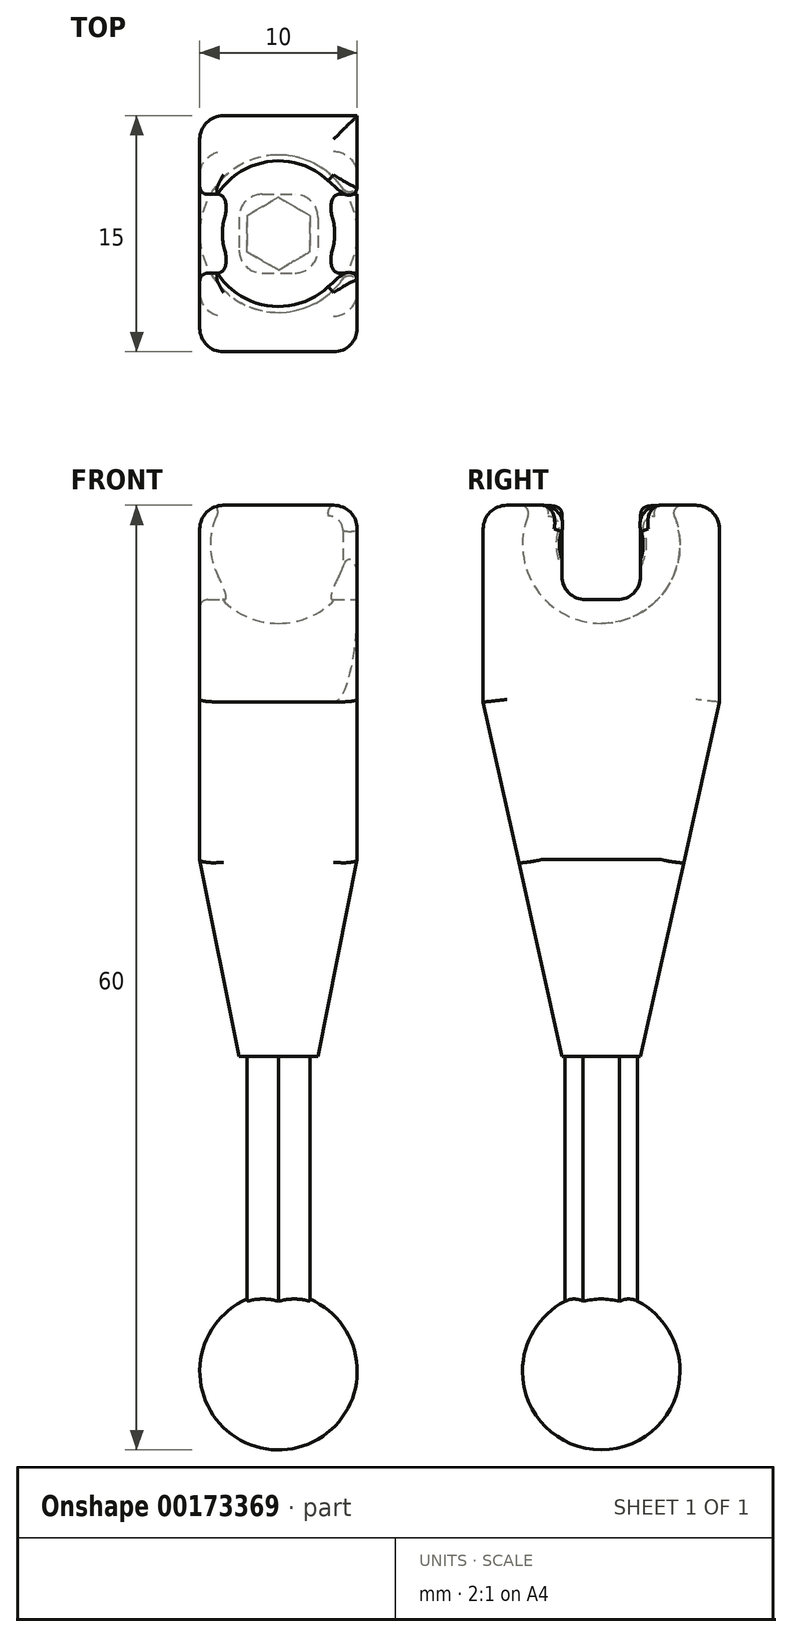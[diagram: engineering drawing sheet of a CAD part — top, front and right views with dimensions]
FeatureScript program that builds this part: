
annotation { "Feature Type Name" : "Feature", "Feature Type Description" : "" }
export const myFeature = defineFeature(function(context is Context, id is Id, definition is map)
    precondition{}
    {
        {
            var Q0;
            Q0=qCreatedBy(makeId("Right.planeOp"),FACE);
            var sketch = newSketch(context, id + "F0", { "sketchPlane" : qUnion([Q0])});
            skLineSegment(sketch, "E0.bottom", {"start": v(-7.5, 50.25) * mm, "end": v(7.5, 50.25) * mm});
            skLineSegment(sketch, "E0.top", {"start": v(-7.5, 15.25) * mm, "end": v(7.5, 15.25) * mm});
            skLineSegment(sketch, "E0.left", {"start": v(-7.5, 50.25) * mm, "end": v(-7.5, 15.25) * mm});
            skLineSegment(sketch, "E0.right", {"start": v(7.5, 50.25) * mm, "end": v(7.5, 15.25) * mm});
            skSolve(sketch);
        }
        {
            var Q0;
            Q0 = qSketchRegion(id + "F0", true);
            extrude(context, id + "F1", {"entities" : qUnion([Q0]), "endBound" : BoundingType.SYMMETRIC, "depth" : 10 * mm});
        }
        {
            var Q0;
            Q0=makeQuery(id+"F1.opExtrude","CAP_FACE",FACE,{"disambiguationData":[OSD([sQuery(id+"F0.wireOp",EDGE,"E0.bottom"),sQuery(id+"F0.wireOp",EDGE,"E0.top"),sQuery(id+"F0.wireOp",EDGE,"E0.left"),sQuery(id+"F0.wireOp",EDGE,"E0.right")])],"isStart":false});
            var sketch = newSketch(context, id + "F2", { "sketchPlane" : qUnion([Q0])});
            skLineSegment(sketch, "E1", {"start": v(-7.5, 15.25) * mm, "end": v(-7.5, 37.75) * mm});
            skLineSegment(sketch, "E2", {"start": v(-7.5, 37.75) * mm, "end": v(-2.5, 15.25) * mm});
            skLineSegment(sketch, "E3", {"start": v(-2.5, 15.25) * mm, "end": v(-7.5, 15.25) * mm});
            skLineSegment(sketch, "E4", {"start": v(0, 50.25) * mm, "end": v(0, 15.25) * mm, "construction": true});
            skLineSegment(sketch, "E5.MirrorCS", {"start": v(7.5, 15.25) * mm, "end": v(7.5, 37.75) * mm});
            skLineSegment(sketch, "E6.MirrorCS", {"start": v(7.5, 37.75) * mm, "end": v(2.5, 15.25) * mm});
            skLineSegment(sketch, "E7.MirrorCS", {"start": v(2.5, 15.25) * mm, "end": v(7.5, 15.25) * mm});
            skSolve(sketch);
        }
        {
            var Q0;
            Q0 = qSketchRegion(id + "F2", true);
            extrude(context, id + "F3", {"entities" : qUnion([Q0]), "operationType" : NewBodyOperationType.REMOVE, "endBound" : BoundingType.SYMMETRIC, "oppositeDirection" : true, "depth" : 25 * mm});
        }
        {
            var Q0;
            Q0=qCreatedBy(makeId("Front.planeOp"),FACE);
            var sketch = newSketch(context, id + "F4", { "sketchPlane" : qUnion([Q0])});
            skLineSegment(sketch, "E8", {"start": v(5, 27.75) * mm, "end": v(5, 15.25) * mm});
            skLineSegment(sketch, "E9", {"start": v(5, 15.25) * mm, "end": v(2.5, 15.25) * mm});
            skLineSegment(sketch, "E10", {"start": v(2.5, 15.25) * mm, "end": v(5, 27.75) * mm});
            skLineSegment(sketch, "E11", {"start": v(0, 10.16) * mm, "end": v(0, 28) * mm, "construction": true});
            skLineSegment(sketch, "E12.MirrorCS", {"start": v(-5, 27.75) * mm, "end": v(-5, 15.25) * mm});
            skLineSegment(sketch, "E13.MirrorCS", {"start": v(-5, 15.25) * mm, "end": v(-2.5, 15.25) * mm});
            skLineSegment(sketch, "E14.MirrorCS", {"start": v(-2.5, 15.25) * mm, "end": v(-5, 27.75) * mm});
            skSolve(sketch);
        }
        {
            var Q0;
            Q0 = qSketchRegion(id + "F4", true);
            extrude(context, id + "F5", {"entities" : qUnion([Q0]), "operationType" : NewBodyOperationType.REMOVE, "endBound" : BoundingType.SYMMETRIC, "oppositeDirection" : true, "depth" : 50 * mm});
        }
        {
            var Q0;
            Q0=makeQuery(id+"F3.boolean.opBoolean","INTERSECT",EDGE,{"derivedFrom":[makeQuery(id+"F1.opExtrude","CAP_FACE",FACE,{"disambiguationData":[OSD([sQuery(id+"F0.wireOp",EDGE,"E0.bottom"),sQuery(id+"F0.wireOp",EDGE,"E0.top"),sQuery(id+"F0.wireOp",EDGE,"E0.left"),sQuery(id+"F0.wireOp",EDGE,"E0.right")])],"isStart":true}),makeQuery(id+"F3.opExtrude","SWEPT_FACE",FACE,{"disambiguationData":[OSD([sQuery(id+"F2.wireOp",EDGE,"E2")])]})]});
            var Q1;
            Q1=makeQuery(id+"F5.boolean.opBoolean","INTERSECT",EDGE,{"derivedFrom":[makeQuery(id+"F3.boolean.opBoolean","COPY",FACE,{"derivedFrom":makeQuery(id+"F3.opExtrude","SWEPT_FACE",FACE,{"disambiguationData":[OSD([sQuery(id+"F2.wireOp",EDGE,"E2")])]})}),makeQuery(id+"F5.opExtrude","SWEPT_FACE",FACE,{"disambiguationData":[OSD([sQuery(id+"F4.wireOp",EDGE,"E14.MirrorCS")])]})]});
            var Q2;
            Q2=makeQuery(id+"F5.boolean.opBoolean","INTERSECT",EDGE,{"derivedFrom":[makeQuery(id+"F3.boolean.opBoolean","COPY",FACE,{"derivedFrom":makeQuery(id+"F3.opExtrude","SWEPT_FACE",FACE,{"disambiguationData":[OSD([sQuery(id+"F2.wireOp",EDGE,"E2")])]})}),makeQuery(id+"F5.opExtrude","SWEPT_FACE",FACE,{"disambiguationData":[OSD([sQuery(id+"F4.wireOp",EDGE,"E10")])]})]});
            var Q3;
            Q3=makeQuery(id+"F3.boolean.opBoolean","INTERSECT",EDGE,{"derivedFrom":[makeQuery(id+"F1.opExtrude","CAP_FACE",FACE,{"disambiguationData":[OSD([sQuery(id+"F0.wireOp",EDGE,"E0.bottom"),sQuery(id+"F0.wireOp",EDGE,"E0.top"),sQuery(id+"F0.wireOp",EDGE,"E0.left"),sQuery(id+"F0.wireOp",EDGE,"E0.right")])],"isStart":false}),makeQuery(id+"F3.opExtrude","SWEPT_FACE",FACE,{"disambiguationData":[OSD([sQuery(id+"F2.wireOp",EDGE,"E2")])]})]});
            var Q4;
            Q4=makeQuery(id+"F1.opExtrude","CAP_EDGE",EDGE,{"disambiguationData":[OSD([sQuery(id+"F0.wireOp",EDGE,"E0.left")])],"isStart":false});
            var Q5;
            Q5=makeQuery(id+"F1.opExtrude","CAP_EDGE",EDGE,{"disambiguationData":[OSD([sQuery(id+"F0.wireOp",EDGE,"E0.left")])],"isStart":true});
            var Q6;
            Q6=makeQuery(id+"F1.opExtrude","CAP_EDGE",EDGE,{"disambiguationData":[OSD([sQuery(id+"F0.wireOp",EDGE,"E0.right")])],"isStart":true});
            var Q7;
            Q7=makeQuery(id+"F3.boolean.opBoolean","INTERSECT",EDGE,{"derivedFrom":[makeQuery(id+"F1.opExtrude","CAP_FACE",FACE,{"disambiguationData":[OSD([sQuery(id+"F0.wireOp",EDGE,"E0.bottom"),sQuery(id+"F0.wireOp",EDGE,"E0.top"),sQuery(id+"F0.wireOp",EDGE,"E0.left"),sQuery(id+"F0.wireOp",EDGE,"E0.right")])],"isStart":true}),makeQuery(id+"F3.opExtrude","SWEPT_FACE",FACE,{"disambiguationData":[OSD([sQuery(id+"F2.wireOp",EDGE,"E6.MirrorCS")])]})]});
            var Q8;
            Q8=makeQuery(id+"F5.boolean.opBoolean","INTERSECT",EDGE,{"derivedFrom":[makeQuery(id+"F3.boolean.opBoolean","COPY",FACE,{"derivedFrom":makeQuery(id+"F3.opExtrude","SWEPT_FACE",FACE,{"disambiguationData":[OSD([sQuery(id+"F2.wireOp",EDGE,"E6.MirrorCS")])]})}),makeQuery(id+"F5.opExtrude","SWEPT_FACE",FACE,{"disambiguationData":[OSD([sQuery(id+"F4.wireOp",EDGE,"E14.MirrorCS")])]})]});
            var Q9;
            Q9=makeQuery(id+"F5.boolean.opBoolean","INTERSECT",EDGE,{"derivedFrom":[makeQuery(id+"F3.boolean.opBoolean","COPY",FACE,{"derivedFrom":makeQuery(id+"F3.opExtrude","SWEPT_FACE",FACE,{"disambiguationData":[OSD([sQuery(id+"F2.wireOp",EDGE,"E6.MirrorCS")])]})}),makeQuery(id+"F5.opExtrude","SWEPT_FACE",FACE,{"disambiguationData":[OSD([sQuery(id+"F4.wireOp",EDGE,"E10")])]})]});
            var Q10;
            Q10=makeQuery(id+"F3.boolean.opBoolean","INTERSECT",EDGE,{"derivedFrom":[makeQuery(id+"F1.opExtrude","CAP_FACE",FACE,{"disambiguationData":[OSD([sQuery(id+"F0.wireOp",EDGE,"E0.bottom"),sQuery(id+"F0.wireOp",EDGE,"E0.top"),sQuery(id+"F0.wireOp",EDGE,"E0.left"),sQuery(id+"F0.wireOp",EDGE,"E0.right")])],"isStart":false}),makeQuery(id+"F3.opExtrude","SWEPT_FACE",FACE,{"disambiguationData":[OSD([sQuery(id+"F2.wireOp",EDGE,"E6.MirrorCS")])]})]});
            var Q11;
            Q11=makeQuery(id+"F3.boolean.opBoolean","COPY",EDGE,{"derivedFrom":makeQuery(id+"F3.opExtrude","SWEPT_EDGE",EDGE,{"disambiguationData":[OSD([sQuery(id+"F0.wireOp",EDGE,"E0.right"),sQuery(id+"F2.wireOp",EDGE,"E5.MirrorCS"),sQuery(id+"F2.wireOp",EDGE,"E6.MirrorCS")])]})});
            var Q12;
            Q12=makeQuery(id+"F3.boolean.opBoolean","COPY",EDGE,{"derivedFrom":makeQuery(id+"F3.opExtrude","SWEPT_EDGE",EDGE,{"disambiguationData":[OSD([sQuery(id+"F0.wireOp",EDGE,"E0.left"),sQuery(id+"F2.wireOp",EDGE,"E1"),sQuery(id+"F2.wireOp",EDGE,"E2")])]})});
            var Q13;
            Q13=makeQuery(id+"F1.opExtrude","SWEPT_EDGE",EDGE,{"disambiguationData":[OSD([sQuery(id+"F0.wireOp",EDGE,"E0.bottom"),sQuery(id+"F0.wireOp",EDGE,"E0.left")])]});
            var Q14;
            Q14=makeQuery(id+"F1.opExtrude","CAP_EDGE",EDGE,{"disambiguationData":[OSD([sQuery(id+"F0.wireOp",EDGE,"E0.bottom")])],"isStart":true});
            var Q15;
            Q15=makeQuery(id+"F1.opExtrude","CAP_EDGE",EDGE,{"disambiguationData":[OSD([sQuery(id+"F0.wireOp",EDGE,"E0.bottom")])],"isStart":false});
            var Q16;
            Q16=makeQuery(id+"F1.opExtrude","SWEPT_EDGE",EDGE,{"disambiguationData":[OSD([sQuery(id+"F0.wireOp",EDGE,"E0.bottom"),sQuery(id+"F0.wireOp",EDGE,"E0.right")])]});
            fillet(context, id + "F6", {"entities" : qUnion([Q0, Q1, Q2, Q3, Q4, Q5, Q6, Q7, Q8, Q9, Q10, Q11, Q12, Q13, Q14, Q15, Q16]), "radius" : 1.5 * mm, "tangentPropagation" : true, "allowEdgeOverflow" : false});
        }
        {
            var Q0;
            Q0=makeQuery(id+"F1.opExtrude","SWEPT_FACE",FACE,{"disambiguationData":[OSD([sQuery(id+"F0.wireOp",EDGE,"E0.top")])]});
            var sketch = newSketch(context, id + "F7", { "sketchPlane" : qUnion([Q0])});
            skCircle(sketch, "E15.cCircle", {"center": v(0, 0) * mm, "radius": 2 * mm, "construction": true});
            skPoint(sketch, "E15.cCircle.perimeterSnap0", {"position": v(2.5, 0) * mm});
            skPoint(sketch, "E15.cCircle.perimeterSnap1", {"position": v(2.09, 0.04) * mm});
            skLineSegment(sketch, "E15.0", {"start": v(2, 1.15) * mm, "end": v(2, -1.15) * mm});
            skLineSegment(sketch, "E15.1", {"start": v(2, -1.15) * mm, "end": v(0, -2.3) * mm});
            skLineSegment(sketch, "E15.2", {"start": v(0, -2.3) * mm, "end": v(-2, -1.15) * mm});
            skLineSegment(sketch, "E15.3", {"start": v(-2, -1.15) * mm, "end": v(-2, 1.15) * mm});
            skLineSegment(sketch, "E15.4", {"start": v(-2, 1.15) * mm, "end": v(0, 2.3) * mm});
            skLineSegment(sketch, "E15.5", {"start": v(0, 2.3) * mm, "end": v(2, 1.15) * mm});
            skPoint(sketch, "E15.0.midPoint", {"position": v(2.09, 0) * mm});
            skPoint(sketch, "E15.0.midPoint.positionSnap0", {"position": v(2.5, 0) * mm});
            skPoint(sketch, "E15.0.midPoint.positionSnap1", {"position": v(2.09, 0.04) * mm});
            skSolve(sketch);
        }
        {
            var Q0;
            Q0 = qSketchRegion(id + "F7", true);
            extrude(context, id + "F8", {"entities" : qUnion([Q0]), "operationType" : NewBodyOperationType.ADD, "depth" : 20 * mm});
        }
        {
            var Q0;
            Q0=makeQuery(id+"F8.opExtrude","CAP_FACE",FACE,{"disambiguationData":[OSD([sQuery(id+"F7.wireOp",EDGE,"E15.0"),sQuery(id+"F7.wireOp",EDGE,"E15.1"),sQuery(id+"F7.wireOp",EDGE,"E15.2"),sQuery(id+"F7.wireOp",EDGE,"E15.3"),sQuery(id+"F7.wireOp",EDGE,"E15.4"),sQuery(id+"F7.wireOp",EDGE,"E15.5")])],"isStart":false});
            var sketch = newSketch(context, id + "F9", { "sketchPlane" : qUnion([Q0])});
            skArc(sketch, "E16", {"start": v(0, 5) * mm, "mid": v(-5, 0) * mm, "end": v(0, -5) * mm});
            skLineSegment(sketch, "E17", {"start": v(0, 5) * mm, "end": v(0, -5) * mm});
            skLineSegment(sketch, "E18", {"start": v(0, 6.34) * mm, "end": v(0, -6.26) * mm, "construction": true});
            skSolve(sketch);
        }
        {
            var Q0;
            {var subQ2=sQuery(id+"F9.wireOp",EDGE,"E16");Q0=makeQuery(id+"F9.imprint","IMPRINT",FACE,{"disambiguationData":[TD([[makeQuery(id+"F9.imprint","IMPRINT",EDGE,{"derivedFrom":subQ2}),1.0]])]});}
            var Q1;
            {var subQ1=makeQuery(id+"F8.opExtrude","CAP_EDGE",EDGE,{"disambiguationData":[OSD([sQuery(id+"F7.wireOp",EDGE,"E15.2")])],"isStart":false});Q1=makeQuery(id+"F9.imprint","IMPRINT",FACE,{"disambiguationData":[TD([[makeQuery(id+"F9.imprint","IMPRINT",EDGE,{"derivedFrom":subQ1}),-1.0]])]});}
            var Q2;
            Q2=sQuery(id+"F9.wireOp",EDGE,"E18");
            revolve(context, id + "F10", {"operationType" : NewBodyOperationType.ADD, "entities" : qUnion([Q0, Q1]), "axis" : qUnion([Q2]), "revolveType" : RevolveType.FULL});
        }
        {
            var Q0;
            Q0=makeQuery(id+"F1.opExtrude","CAP_FACE",FACE,{"disambiguationData":[OSD([sQuery(id+"F0.wireOp",EDGE,"E0.bottom"),sQuery(id+"F0.wireOp",EDGE,"E0.top"),sQuery(id+"F0.wireOp",EDGE,"E0.left"),sQuery(id+"F0.wireOp",EDGE,"E0.right")])],"isStart":false});
            var sketch = newSketch(context, id + "F11", { "sketchPlane" : qUnion([Q0])});
            skLineSegment(sketch, "E19.bottom", {"start": v(-2.5, 50.25) * mm, "end": v(2.5, 50.25) * mm});
            skLineSegment(sketch, "E19.top", {"start": v(-1, 44.25) * mm, "end": v(1, 44.25) * mm});
            skLineSegment(sketch, "E19.left", {"start": v(-2.5, 50.25) * mm, "end": v(-2.5, 45.75) * mm});
            skLineSegment(sketch, "E19.right", {"start": v(2.5, 50.25) * mm, "end": v(2.5, 45.75) * mm});
            skPoint(sketch, "E20.visualSharp", {"position": v(-2.5, 44.25) * mm});
            skArc(sketch, "E20.filletArc", {"start": v(-2.5, 45.75) * mm, "mid": v(-2.06, 44.69) * mm, "end": v(-1, 44.25) * mm});
            skPoint(sketch, "E21.visualSharp", {"position": v(2.5, 44.25) * mm});
            skArc(sketch, "E21.filletArc", {"start": v(1, 44.25) * mm, "mid": v(2.06, 44.69) * mm, "end": v(2.5, 45.75) * mm});
            skSolve(sketch);
        }
        {
            var Q0;
            Q0 = qSketchRegion(id + "F11", true);
            extrude(context, id + "F12", {"entities" : qUnion([Q0]), "operationType" : NewBodyOperationType.REMOVE, "endBound" : BoundingType.THROUGH_ALL, "oppositeDirection" : true, "depth" : 25 * mm});
        }
        {
            var Q0;
            Q0=qCreatedBy(makeId("Right.planeOp"),FACE);
            var sketch = newSketch(context, id + "F13", { "sketchPlane" : qUnion([Q0])});
            skLineSegment(sketch, "E22", {"start": v(0, 52.75) * mm, "end": v(0, 42.75) * mm});
            skLineSegment(sketch, "E23", {"start": v(0, 54.58) * mm, "end": v(0, 40) * mm, "construction": true});
            skPoint(sketch, "E24.center.orphan", {"position": v(0, 47.75) * mm});
            skArc(sketch, "E25", {"start": v(0, 52.75) * mm, "mid": v(-5, 47.75) * mm, "end": v(0, 42.75) * mm});
            skSolve(sketch);
        }
        {
            var Q0;
            Q0 = qSketchRegion(id + "F13", true);
            var Q1;
            Q1=sQuery(id+"F13.wireOp",EDGE,"E23");
            revolve(context, id + "F14", {"operationType" : NewBodyOperationType.REMOVE, "entities" : qUnion([Q0]), "axis" : qUnion([Q1]), "revolveType" : RevolveType.FULL, "oppositeDirection" : true});
        }
        {
            var Q0;
            Q0=makeQuery(id+"F12.boolean.opBoolean","COPY",EDGE,{"derivedFrom":makeQuery(id+"F12.opExtrude","CAP_EDGE",EDGE,{"disambiguationData":[OSD([sQuery(id+"F11.wireOp",EDGE,"E19.left")])],"isStart":true})});
            var Q1;
            {var subQ0=sQuery(id+"F0.wireOp",EDGE,"E0.bottom");Q1=makeQuery(id+"F14.boolean.opBoolean","INTERSECT",EDGE,{"derivedFrom":[makeQuery(id+"F12.boolean.opBoolean","SPLIT",FACE,{"disambiguationData":[TD([makeQuery(id+"F12.opExtrude","SWEPT_FACE",FACE,{"disambiguationData":[OSD([sQuery(id+"F11.wireOp",EDGE,"E19.right")])]})])],"derivedFrom":makeQuery(id+"F1.opExtrude","SWEPT_FACE",FACE,{"disambiguationData":[OSD([subQ0])]})}),makeQuery(id+"F14.opRevolve","SWEPT_FACE",FACE,{"disambiguationData":[OSD([sQuery(id+"F13.wireOp",EDGE,"E25")])]})]});}
            var Q2;
            {var subQ0=sQuery(id+"F0.wireOp",EDGE,"E0.bottom");Q2=makeQuery(id+"F14.boolean.opBoolean","INTERSECT",EDGE,{"derivedFrom":[makeQuery(id+"F12.boolean.opBoolean","SPLIT",FACE,{"disambiguationData":[TD([makeQuery(id+"F12.opExtrude","SWEPT_FACE",FACE,{"disambiguationData":[OSD([sQuery(id+"F11.wireOp",EDGE,"E19.left")])]})])],"derivedFrom":makeQuery(id+"F1.opExtrude","SWEPT_FACE",FACE,{"disambiguationData":[OSD([subQ0])]})}),makeQuery(id+"F14.opRevolve","SWEPT_FACE",FACE,{"disambiguationData":[OSD([sQuery(id+"F13.wireOp",EDGE,"E25")])]})]});}
            var Q3;
            Q3=makeQuery(id+"F12.boolean.opBoolean","INTERSECT",EDGE,{"derivedFrom":[makeQuery(id+"F1.opExtrude","CAP_FACE",FACE,{"disambiguationData":[OSD([sQuery(id+"F0.wireOp",EDGE,"E0.bottom"),sQuery(id+"F0.wireOp",EDGE,"E0.top"),sQuery(id+"F0.wireOp",EDGE,"E0.left"),sQuery(id+"F0.wireOp",EDGE,"E0.right")])],"isStart":true}),makeQuery(id+"F12.opExtrude","SWEPT_FACE",FACE,{"disambiguationData":[OSD([sQuery(id+"F11.wireOp",EDGE,"E20.filletArc")])]})]});
            fillet(context, id + "F15", {"entities" : qUnion([Q0, Q1, Q2, Q3]), "radius" : 0.5 * mm, "tangentPropagation" : true, "allowEdgeOverflow" : false});
        }
    });
